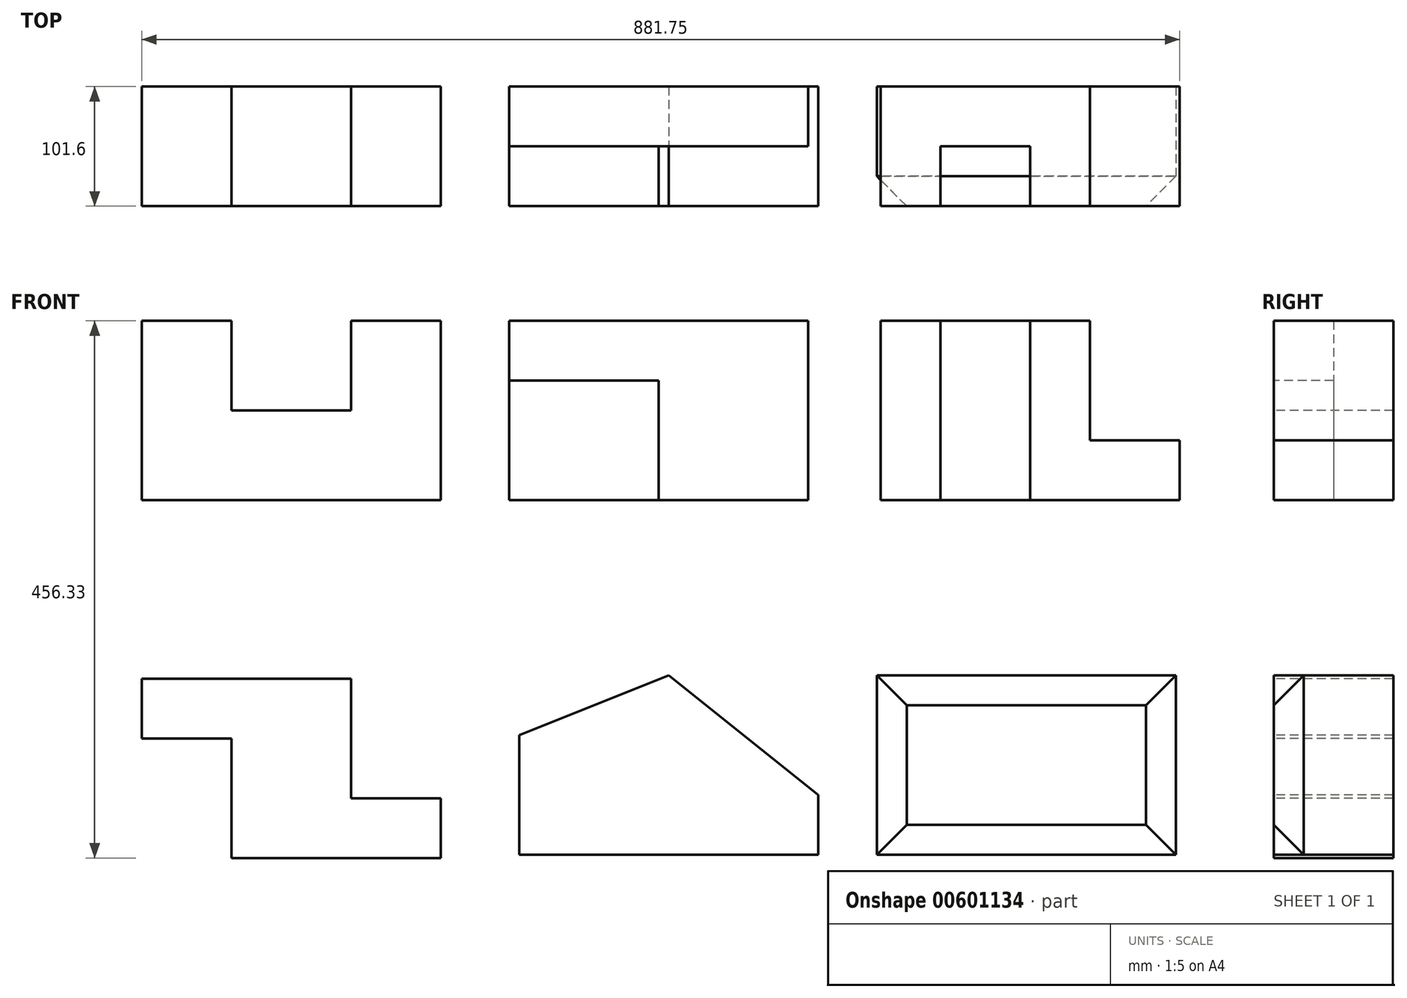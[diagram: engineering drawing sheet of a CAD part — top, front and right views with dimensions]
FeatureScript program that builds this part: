
annotation { "Feature Type Name" : "Feature", "Feature Type Description" : "" }
export const myFeature = defineFeature(function(context is Context, id is Id, definition is map)
    precondition{}
    {
        {
            var Q0;
            Q0=qCreatedBy(makeId("Front.planeOp"),FACE);
            var sketch = newSketch(context, id + "F0", { "sketchPlane" : qUnion([Q0])});
            skLineSegment(sketch, "E0", {"start": v(0, 0) * mm, "end": v(254, 0) * mm});
            skLineSegment(sketch, "E1", {"start": v(254, 0) * mm, "end": v(254, 152.4) * mm});
            skLineSegment(sketch, "E2", {"start": v(254, 152.4) * mm, "end": v(177.8, 152.4) * mm});
            skLineSegment(sketch, "E3", {"start": v(177.8, 152.4) * mm, "end": v(177.8, 76.2) * mm});
            skLineSegment(sketch, "E4", {"start": v(177.8, 76.2) * mm, "end": v(76.2, 76.2) * mm});
            skLineSegment(sketch, "E5", {"start": v(76.2, 76.2) * mm, "end": v(76.2, 152.4) * mm});
            skLineSegment(sketch, "E6", {"start": v(76.2, 152.4) * mm, "end": v(0, 152.4) * mm});
            skLineSegment(sketch, "E7", {"start": v(0, 152.4) * mm, "end": v(0, 0) * mm});
            skSolve(sketch);
        }
        {
            var Q0;
            Q0=makeQuery(id+"F0.imprint","IMPRINT",FACE,{"disambiguationData":[TD([[makeQuery(id+"F0.imprint","IMPRINT",EDGE,{"derivedFrom":sQuery(id+"F0.wireOp",EDGE,"E0")}),1.0]])]});
            extrude(context, id + "F1", {"entities" : qUnion([Q0]), "oppositeDirection" : true, "depth" : 101.6 * mm, "offsetDistance" : 25.4 * mm});
        }
        {
            var Q0;
            Q0=qCreatedBy(makeId("Top.planeOp"),FACE);
            var sketch = newSketch(context, id + "F2", { "sketchPlane" : qUnion([Q0])});
            skLineSegment(sketch, "E8", {"start": v(312.16, 0) * mm, "end": v(312.16, 101.6) * mm});
            skLineSegment(sketch, "E9", {"start": v(312.16, 101.6) * mm, "end": v(566.16, 101.6) * mm});
            skLineSegment(sketch, "E10", {"start": v(566.16, 101.6) * mm, "end": v(566.16, 50.8) * mm});
            skLineSegment(sketch, "E11", {"start": v(566.16, 50.8) * mm, "end": v(439.16, 50.8) * mm});
            skLineSegment(sketch, "E12", {"start": v(312.16, 0) * mm, "end": v(439.16, 0) * mm});
            skLineSegment(sketch, "E13", {"start": v(439.16, 50.8) * mm, "end": v(439.16, 0) * mm});
            skSolve(sketch);
        }
        {
            var Q0;
            Q0=makeQuery(id+"F2.imprint","IMPRINT",FACE,{"disambiguationData":[TD([[makeQuery(id+"F2.imprint","IMPRINT",EDGE,{"derivedFrom":sQuery(id+"F2.wireOp",EDGE,"E8")}),-1.0]])]});
            extrude(context, id + "F3", {"entities" : qUnion([Q0]), "depth" : 152.4 * mm, "offsetDistance" : 25.4 * mm});
        }
        {
            var Q0;
            Q0=makeQuery(id+"F3.opExtrude","SWEPT_FACE",FACE,{"disambiguationData":[OSD([sQuery(id+"F2.wireOp",EDGE,"E12")])]});
            var sketch = newSketch(context, id + "F4", { "sketchPlane" : qUnion([Q0])});
            skLineSegment(sketch, "E14.bottom", {"start": v(312.16, 152.4) * mm, "end": v(439.16, 152.4) * mm});
            skLineSegment(sketch, "E14.top", {"start": v(312.16, 101.6) * mm, "end": v(439.16, 101.6) * mm});
            skLineSegment(sketch, "E14.left", {"start": v(312.16, 152.4) * mm, "end": v(312.16, 101.6) * mm});
            skLineSegment(sketch, "E14.right", {"start": v(439.16, 152.4) * mm, "end": v(439.16, 101.6) * mm});
            skSolve(sketch);
        }
        {
            var Q0;
            Q0=qSketchRegion(id+"F4",true);
            extrude(context, id + "F5", {"entities" : qUnion([Q0]), "operationType" : NewBodyOperationType.ADD, "oppositeDirection" : true, "depth" : 50.8 * mm, "offsetDistance" : 25.4 * mm});
        }
        {
            var Q0;
            Q0=makeQuery(id+"F3.opExtrude","SWEPT_FACE",FACE,{"disambiguationData":[OSD([sQuery(id+"F2.wireOp",EDGE,"E12")])]});
            var sketch = newSketch(context, id + "F6", { "sketchPlane" : qUnion([Q0])});
            skLineSegment(sketch, "E15.bottom", {"start": v(312.16, 152.4) * mm, "end": v(439.16, 152.4) * mm});
            skLineSegment(sketch, "E15.top", {"start": v(312.16, 101.6) * mm, "end": v(439.16, 101.6) * mm});
            skLineSegment(sketch, "E15.left", {"start": v(312.16, 152.4) * mm, "end": v(312.16, 101.6) * mm});
            skLineSegment(sketch, "E15.right", {"start": v(439.16, 152.4) * mm, "end": v(439.16, 101.6) * mm});
            skSolve(sketch);
        }
        {
            var Q0;
            Q0=qSketchRegion(id+"F6",true);
            extrude(context, id + "F7", {"entities" : qUnion([Q0]), "operationType" : NewBodyOperationType.REMOVE, "oppositeDirection" : true, "depth" : 50.8 * mm, "offsetDistance" : 25.4 * mm});
        }
        {
            var Q0;
            Q0=makeQuery(id+"F3.opExtrude","SWEPT_FACE",FACE,{"disambiguationData":[OSD([sQuery(id+"F2.wireOp",EDGE,"E12")])]});
            var sketch = newSketch(context, id + "F8", { "sketchPlane" : qUnion([Q0])});
            skLineSegment(sketch, "E16", {"start": v(627.75, 0) * mm, "end": v(627.75, 152.4) * mm});
            skLineSegment(sketch, "E17", {"start": v(627.75, 152.4) * mm, "end": v(805.55, 152.4) * mm});
            skLineSegment(sketch, "E18", {"start": v(805.55, 152.4) * mm, "end": v(805.55, 50.8) * mm});
            skLineSegment(sketch, "E19", {"start": v(805.55, 50.8) * mm, "end": v(881.75, 50.8) * mm});
            skLineSegment(sketch, "E20", {"start": v(881.75, 50.8) * mm, "end": v(881.75, 0) * mm});
            skLineSegment(sketch, "E21", {"start": v(881.75, 0) * mm, "end": v(627.75, 0) * mm});
            skSolve(sketch);
        }
        {
            var Q0;
            Q0=makeQuery(id+"F8.imprint","IMPRINT",FACE,{"disambiguationData":[TD([[makeQuery(id+"F8.imprint","IMPRINT",EDGE,{"derivedFrom":sQuery(id+"F8.wireOp",EDGE,"E16")}),-1.0]])]});
            extrude(context, id + "F9", {"entities" : qUnion([Q0]), "oppositeDirection" : true, "depth" : 101.6 * mm, "offsetDistance" : 25.4 * mm});
        }
        {
            var Q0;
            Q0=makeQuery(id+"F9.opExtrude","SWEPT_FACE",FACE,{"disambiguationData":[OSD([sQuery(id+"F8.wireOp",EDGE,"E17")])]});
            var sketch = newSketch(context, id + "F10", { "sketchPlane" : qUnion([Q0])});
            skLineSegment(sketch, "E22.bottom", {"start": v(678.55, 0) * mm, "end": v(754.75, 0) * mm});
            skLineSegment(sketch, "E22.top", {"start": v(678.55, 50.8) * mm, "end": v(754.75, 50.8) * mm});
            skLineSegment(sketch, "E22.left", {"start": v(678.55, 0) * mm, "end": v(678.55, 50.8) * mm});
            skLineSegment(sketch, "E22.right", {"start": v(754.75, 0) * mm, "end": v(754.75, 50.8) * mm});
            skSolve(sketch);
        }
        {
            var Q0;
            Q0=makeQuery(id+"F10.imprint","IMPRINT",FACE,{"disambiguationData":[TD([[makeQuery(id+"F10.imprint","IMPRINT",EDGE,{"derivedFrom":sQuery(id+"F10.wireOp",EDGE,"E22.bottom")}),1.0]])]});
            extrude(context, id + "F11", {"entities" : qUnion([Q0]), "operationType" : NewBodyOperationType.REMOVE, "oppositeDirection" : true, "depth" : 152.4 * mm, "offsetDistance" : 25.4 * mm});
        }
        {
            var Q0;
            Q0=qCreatedBy(makeId("Front.planeOp"),FACE);
            var sketch = newSketch(context, id + "F12", { "sketchPlane" : qUnion([Q0])});
            skLineSegment(sketch, "E23", {"start": v(0, -151.53) * mm, "end": v(177.8, -151.53) * mm});
            skLineSegment(sketch, "E24", {"start": v(177.8, -151.53) * mm, "end": v(177.8, -253.13) * mm});
            skLineSegment(sketch, "E25", {"start": v(177.8, -253.13) * mm, "end": v(254, -253.13) * mm});
            skLineSegment(sketch, "E26", {"start": v(254, -253.13) * mm, "end": v(254, -303.93) * mm});
            skLineSegment(sketch, "E27", {"start": v(254, -303.93) * mm, "end": v(76.2, -303.93) * mm});
            skLineSegment(sketch, "E28", {"start": v(76.2, -303.93) * mm, "end": v(76.2, -202.33) * mm});
            skLineSegment(sketch, "E29", {"start": v(76.2, -202.33) * mm, "end": v(0, -202.33) * mm});
            skLineSegment(sketch, "E30", {"start": v(0, -202.33) * mm, "end": v(0, -151.53) * mm});
            skSolve(sketch);
        }
        {
            var Q0;
            Q0=makeQuery(id+"F12.imprint","IMPRINT",FACE,{"disambiguationData":[TD([[makeQuery(id+"F12.imprint","IMPRINT",EDGE,{"derivedFrom":sQuery(id+"F12.wireOp",EDGE,"E23")}),-1.0]])]});
            extrude(context, id + "F13", {"entities" : qUnion([Q0]), "oppositeDirection" : true, "depth" : 101.6 * mm, "offsetDistance" : 25.4 * mm});
        }
        {
            var Q0;
            Q0=qCreatedBy(makeId("Front.planeOp"),FACE);
            var sketch = newSketch(context, id + "F14", { "sketchPlane" : qUnion([Q0])});
            skLineSegment(sketch, "E31", {"start": v(320.72, -301.32) * mm, "end": v(574.72, -301.32) * mm});
            skLineSegment(sketch, "E32", {"start": v(574.72, -301.32) * mm, "end": v(574.72, -250.52) * mm});
            skLineSegment(sketch, "E33", {"start": v(574.72, -250.52) * mm, "end": v(447.72, -148.92) * mm});
            skLineSegment(sketch, "E34", {"start": v(320.72, -301.32) * mm, "end": v(320.72, -199.72) * mm});
            skLineSegment(sketch, "E35", {"start": v(320.72, -199.72) * mm, "end": v(447.72, -148.92) * mm});
            skSolve(sketch);
        }
        {
            var Q0;
            Q0=makeQuery(id+"F14.imprint","IMPRINT",FACE,{"disambiguationData":[TD([[makeQuery(id+"F14.imprint","IMPRINT",EDGE,{"derivedFrom":sQuery(id+"F14.wireOp",EDGE,"E31")}),1.0]])]});
            extrude(context, id + "F15", {"entities" : qUnion([Q0]), "oppositeDirection" : true, "depth" : 101.6 * mm, "offsetDistance" : 25.4 * mm});
        }
        {
            var Q0;
            Q0=qCreatedBy(makeId("Front.planeOp"),FACE);
            var sketch = newSketch(context, id + "F16", { "sketchPlane" : qUnion([Q0])});
            skLineSegment(sketch, "E36", {"start": v(624.5, -301.15) * mm, "end": v(624.5, -148.75) * mm});
            skLineSegment(sketch, "E37", {"start": v(624.5, -148.75) * mm, "end": v(878.5, -148.75) * mm});
            skLineSegment(sketch, "E38", {"start": v(624.5, -301.15) * mm, "end": v(878.5, -301.15) * mm});
            skLineSegment(sketch, "E39", {"start": v(878.5, -301.15) * mm, "end": v(878.5, -148.75) * mm});
            skSolve(sketch);
        }
        {
            var Q0;
            Q0=makeQuery(id+"F16.imprint","IMPRINT",FACE,{"disambiguationData":[TD([[makeQuery(id+"F16.imprint","IMPRINT",EDGE,{"derivedFrom":sQuery(id+"F16.wireOp",EDGE,"E36")}),-1.0]])]});
            extrude(context, id + "F17", {"entities" : qUnion([Q0]), "oppositeDirection" : true, "depth" : 101.6 * mm, "offsetDistance" : 25.4 * mm});
        }
        {
            var Q0;
            Q0=makeQuery(id+"F17.opExtrude","CAP_FACE",FACE,{"disambiguationData":[OSD([sQuery(id+"F16.wireOp",EDGE,"E36"),sQuery(id+"F16.wireOp",EDGE,"E37"),sQuery(id+"F16.wireOp",EDGE,"E38"),sQuery(id+"F16.wireOp",EDGE,"E39")])],"isStart":true});
            chamfer(context, id + "F18", {"entities" : qUnion([Q0]), "width" : 25.4 * mm, "tangentPropagation" : true});
        }
    });
